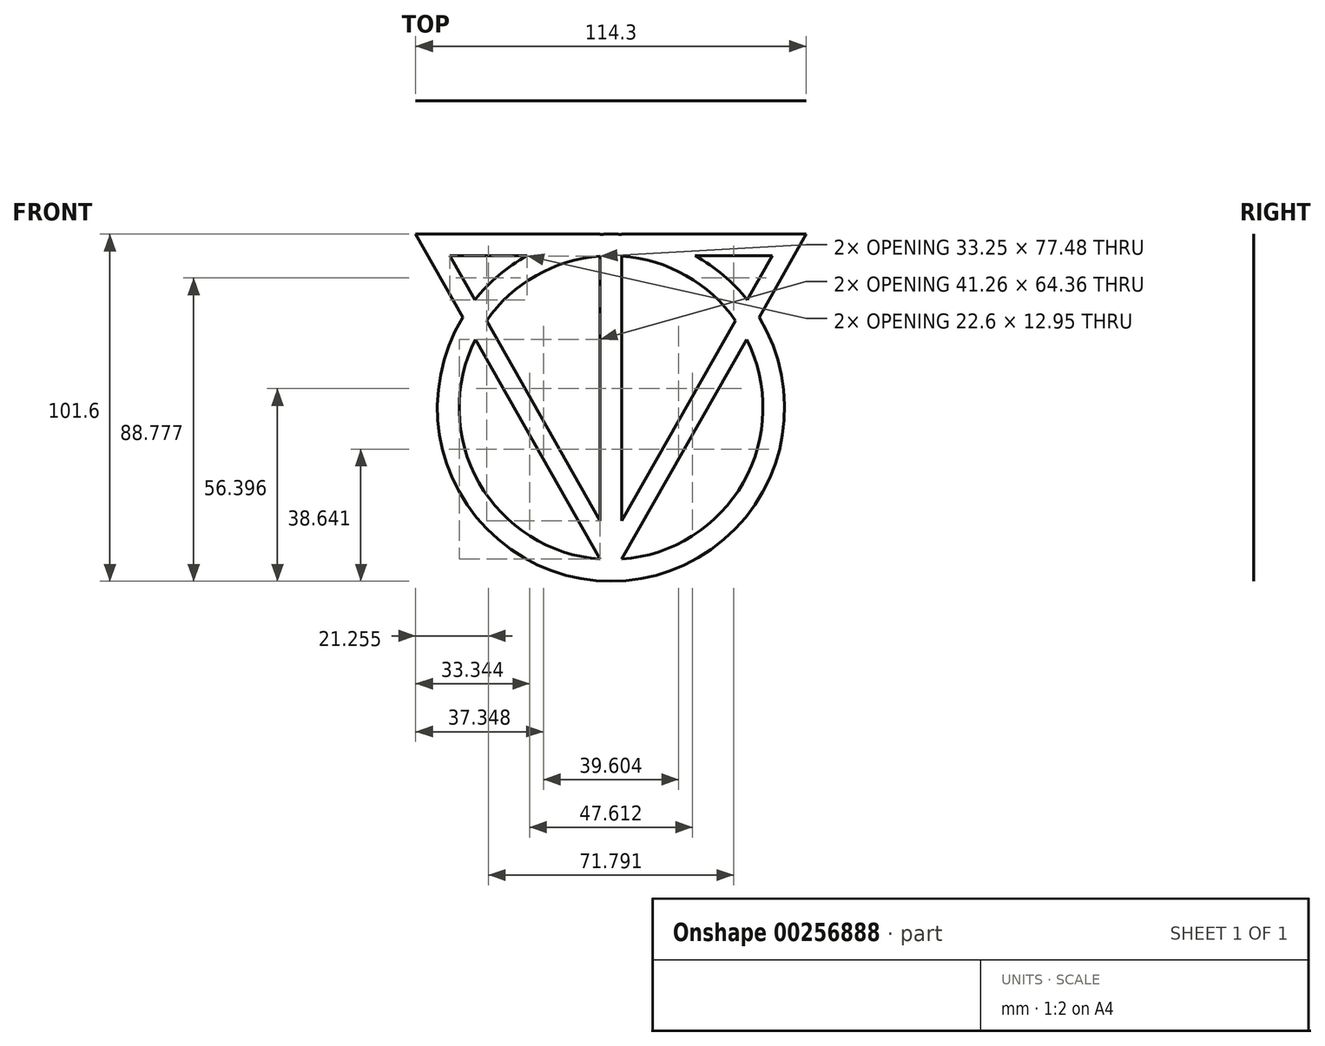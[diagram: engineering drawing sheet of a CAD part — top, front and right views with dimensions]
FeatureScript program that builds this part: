
annotation { "Feature Type Name" : "Feature", "Feature Type Description" : "" }
export const myFeature = defineFeature(function(context is Context, id is Id, definition is map)
    precondition{}
    {
        {
            var Q0;
            Q0=qCreatedBy(makeId("Front.planeOp"),FACE);
            var sketch = newSketch(context, id + "F0", { "sketchPlane" : qUnion([Q0])});
            skArc(sketch, "E0", {"start": v(0, -50.8) * mm, "mid": v(44.3, -24.85) * mm, "end": v(43.35, 26.48) * mm});
            skArc(sketch, "E1", {"start": v(3.18, -44.34) * mm, "mid": v(38.66, -21.93) * mm, "end": v(39.69, 20.02) * mm});
            skPoint(sketch, "E2", {"position": v(0, 50.8) * mm});
            skPoint(sketch, "E3", {"position": v(0, -44.45) * mm});
            skLineSegment(sketch, "E4", {"start": v(0, 50.8) * mm, "end": v(50.8, 50.8) * mm});
            skPoint(sketch, "E5", {"position": v(3.17, 50.8) * mm});
            skPoint(sketch, "E6", {"position": v(-3.18, 50.8) * mm});
            skLineSegment(sketch, "E7", {"start": v(50.8, 50.8) * mm, "end": v(57.15, 50.8) * mm});
            skLineSegment(sketch, "E8", {"start": v(3.18, 50.8) * mm, "end": v(3.18, 50.7) * mm});
            skLineSegment(sketch, "E9", {"start": v(-3.18, 50.8) * mm, "end": v(-3.18, 50.7) * mm});
            skLineSegment(sketch, "E10.trimOffspring", {"start": v(3.18, 44.45) * mm, "end": v(3.18, -33.14) * mm});
            skLineSegment(sketch, "E11.trimOffspring", {"start": v(24.6, 44.45) * mm, "end": v(47.2, 44.45) * mm});
            skArc(sketch, "E12.trimOffspring", {"start": v(3.18, 50.7) * mm, "mid": v(1.59, 50.78) * mm, "end": v(0, 50.8) * mm});
            skLineSegment(sketch, "E13", {"start": v(3.18, -44.34) * mm, "end": v(39.69, 20.02) * mm});
            skPoint(sketch, "E14.end.orphan", {"position": v(50.8, 44.45) * mm});
            skPoint(sketch, "E15.orphan", {"position": v(53.55, 44.45) * mm});
            skLineSegment(sketch, "E16", {"start": v(47.2, 44.45) * mm, "end": v(39.85, 31.5) * mm});
            skLineSegment(sketch, "E17.trimOffspring", {"start": v(43.35, 26.48) * mm, "end": v(57.15, 50.8) * mm});
            skLineSegment(sketch, "E18.trimOffspring", {"start": v(36.43, 25.47) * mm, "end": v(3.18, -33.14) * mm});
            skArc(sketch, "E19.trimOffspring", {"start": v(36.43, 25.47) * mm, "mid": v(21.93, 38.66) * mm, "end": v(3.18, 44.34) * mm});
            skArc(sketch, "E20.trimOffspring", {"start": v(39.85, 31.5) * mm, "mid": v(32.87, 38.74) * mm, "end": v(24.6, 44.45) * mm});
            skLineSegment(sketch, "E21.MirrorCS", {"start": v(-3.17, 50.8) * mm, "end": v(-3.17, 50.7) * mm});
            skArc(sketch, "E22.MirrorCS", {"start": v(-3.17, 50.7) * mm, "mid": v(-1.59, 50.78) * mm, "end": v(0, 50.8) * mm});
            skLineSegment(sketch, "E23.MirrorCS", {"start": v(-3.17, 44.45) * mm, "end": v(-3.17, -33.14) * mm});
            skLineSegment(sketch, "E24.MirrorCS", {"start": v(-24.6, 44.45) * mm, "end": v(-47.2, 44.45) * mm});
            skLineSegment(sketch, "E25.MirrorCS", {"start": v(-47.2, 44.45) * mm, "end": v(-39.85, 31.5) * mm});
            skLineSegment(sketch, "E26.MirrorCS", {"start": v(-43.35, 26.48) * mm, "end": v(-57.15, 50.8) * mm});
            skLineSegment(sketch, "E27.MirrorCS", {"start": v(-36.43, 25.47) * mm, "end": v(-3.17, -33.14) * mm});
            skPoint(sketch, "E28.MirrorP", {"position": v(-53.55, 44.45) * mm});
            skArc(sketch, "E29.MirrorCS", {"start": v(-36.43, 25.47) * mm, "mid": v(-21.93, 38.66) * mm, "end": v(-3.17, 44.34) * mm});
            skArc(sketch, "E30.MirrorCS", {"start": v(-39.85, 31.5) * mm, "mid": v(-32.87, 38.74) * mm, "end": v(-24.6, 44.45) * mm});
            skArc(sketch, "E31.MirrorCS", {"start": v(0, -50.8) * mm, "mid": v(-44.3, -24.85) * mm, "end": v(-43.35, 26.48) * mm});
            skArc(sketch, "E32.MirrorCS", {"start": v(-3.17, -44.34) * mm, "mid": v(-38.66, -21.93) * mm, "end": v(-39.69, 20.02) * mm});
            skLineSegment(sketch, "E33.MirrorCS", {"start": v(0, 50.8) * mm, "end": v(-50.8, 50.8) * mm});
            skLineSegment(sketch, "E34.MirrorCS", {"start": v(-3.17, -44.34) * mm, "end": v(-39.69, 20.02) * mm});
            skLineSegment(sketch, "E35.MirrorCS", {"start": v(-50.8, 50.8) * mm, "end": v(-57.15, 50.8) * mm});
            skPoint(sketch, "E36.MirrorP", {"position": v(-50.8, 44.45) * mm});
            skPoint(sketch, "E37.MirrorP", {"position": v(3.18, 50.8) * mm});
            skPoint(sketch, "E38.orphan", {"position": v(0, 44.45) * mm});
            skSolve(sketch);
        }
        {
            var Q0;
            Q0=makeQuery(id+"F0.imprint","IMPRINT",FACE,{"disambiguationData":[TD([[makeQuery(id+"F0.imprint","IMPRINT",EDGE,{"derivedFrom":sQuery(id+"F0.wireOp",EDGE,"E0")}),1.0]])]});
            extrude(context, id + "F1", {"entities" : qUnion([Q0]), "depth" : 1 / 203.2 * mm});
        }
    });
